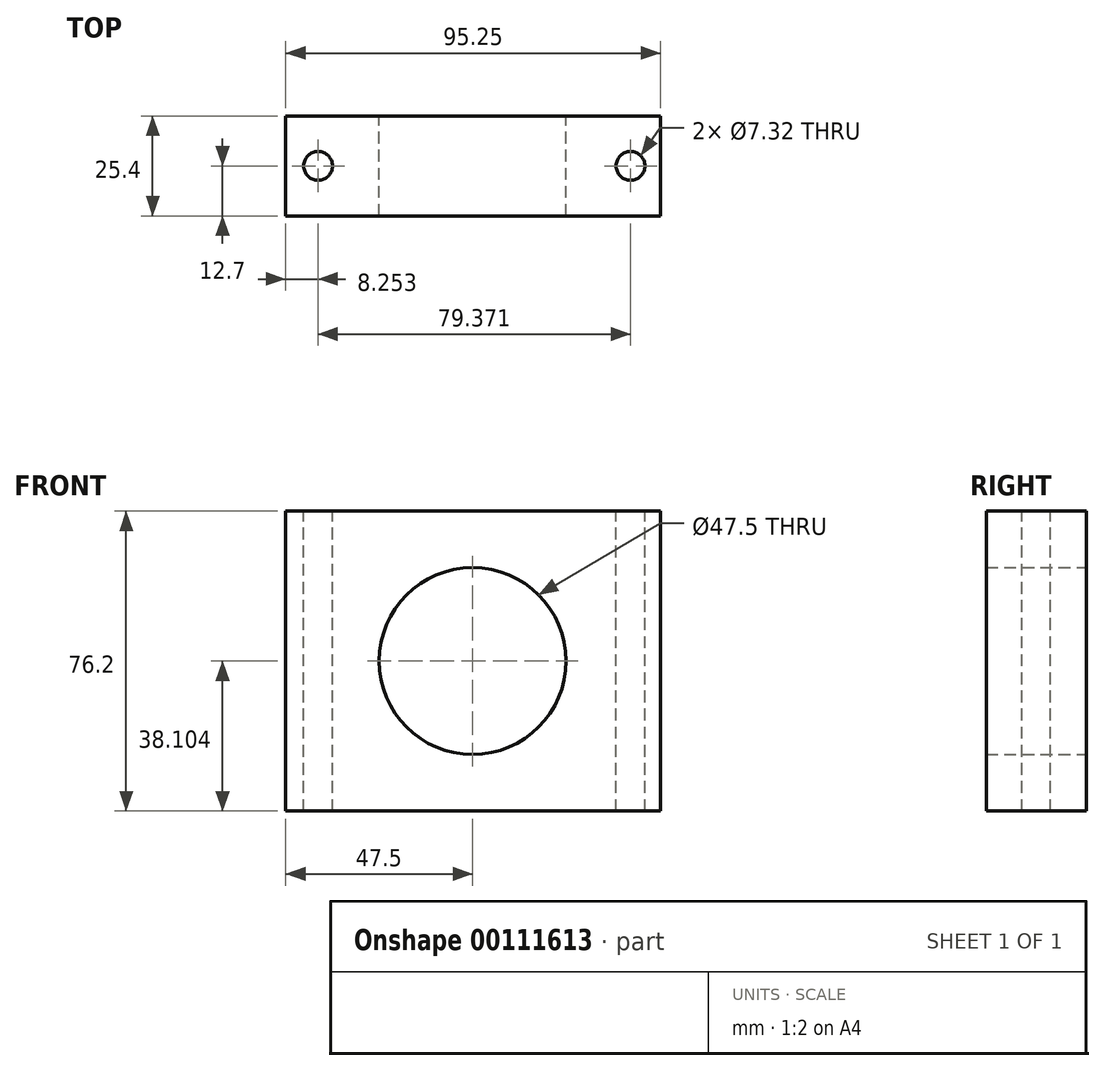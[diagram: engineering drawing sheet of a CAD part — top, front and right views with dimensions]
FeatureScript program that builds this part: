
annotation { "Feature Type Name" : "Feature", "Feature Type Description" : "" }
export const myFeature = defineFeature(function(context is Context, id is Id, definition is map)
    precondition{}
    {
        {
            var Q0;
            Q0=qCreatedBy(makeId("Front.planeOp"),FACE);
            var sketch = newSketch(context, id + "F0", { "sketchPlane" : qUnion([Q0])});
            skLineSegment(sketch, "E0", {"start": v(-32.78, -30.83) * mm, "end": v(-32.78, 45.37) * mm});
            skLineSegment(sketch, "E1", {"start": v(-32.78, 45.37) * mm, "end": v(62.47, 45.37) * mm});
            skLineSegment(sketch, "E2", {"start": v(62.47, 45.37) * mm, "end": v(62.47, -30.83) * mm});
            skLineSegment(sketch, "E3", {"start": v(62.47, -30.83) * mm, "end": v(-32.78, -30.83) * mm});
            skCircle(sketch, "E4", {"center": v(14.72, 7.27) * mm, "radius": 23.75 * mm});
            skSolve(sketch);
        }
        {
            var Q0;
            Q0=makeQuery(id+"F0.imprint","IMPRINT",FACE,{"disambiguationData":[TD([[makeQuery(id+"F0.imprint","IMPRINT",EDGE,{"derivedFrom":sQuery(id+"F0.wireOp",EDGE,"E0")}),-1.0]])]});
            extrude(context, id + "F1", {"entities" : qUnion([Q0]), "depth" : 25.4 * mm});
        }
        {
            var Q0;
            Q0=makeQuery(id+"F1.opExtrude","SWEPT_FACE",FACE,{"disambiguationData":[OSD([sQuery(id+"F0.wireOp",EDGE,"E1")])]});
            var sketch = newSketch(context, id + "F2", { "sketchPlane" : qUnion([Q0])});
            skCircle(sketch, "E5", {"center": v(-24.53, -12.7) * mm, "radius": 1.84 * mm});
            skCircle(sketch, "E6", {"center": v(54.84, -12.7) * mm, "radius": 1.33 * mm});
            skSolve(sketch);
        }
        {
            var Q0;
            Q0=sQuery(id+"F2.wireOp",VERTEX,"E5.center");
            var Q1;
            Q1=sQuery(id+"F2.wireOp",VERTEX,"E6.center");
            var Q2;
            Q2=makeQuery(id+"F1.opExtrude","SWEPT_BODY",BODY,{"disambiguationData":[OSD([sQuery(id+"F0.wireOp",EDGE,"E0"),sQuery(id+"F0.wireOp",EDGE,"E1"),sQuery(id+"F0.wireOp",EDGE,"E2"),sQuery(id+"F0.wireOp",EDGE,"E3"),sQuery(id+"F0.wireOp",EDGE,"E4")])]});
            hole(context, id + "F3", {"style" : HoleStyle.SIMPLE, "endStyle" : HoleEndStyle.THROUGH, "holeDiameter" : 7.32 * mm, "locations" : qUnion([Q0, Q1]), "scope" : qUnion([Q2]), "isTappedThrough" : true});
        }
    });
